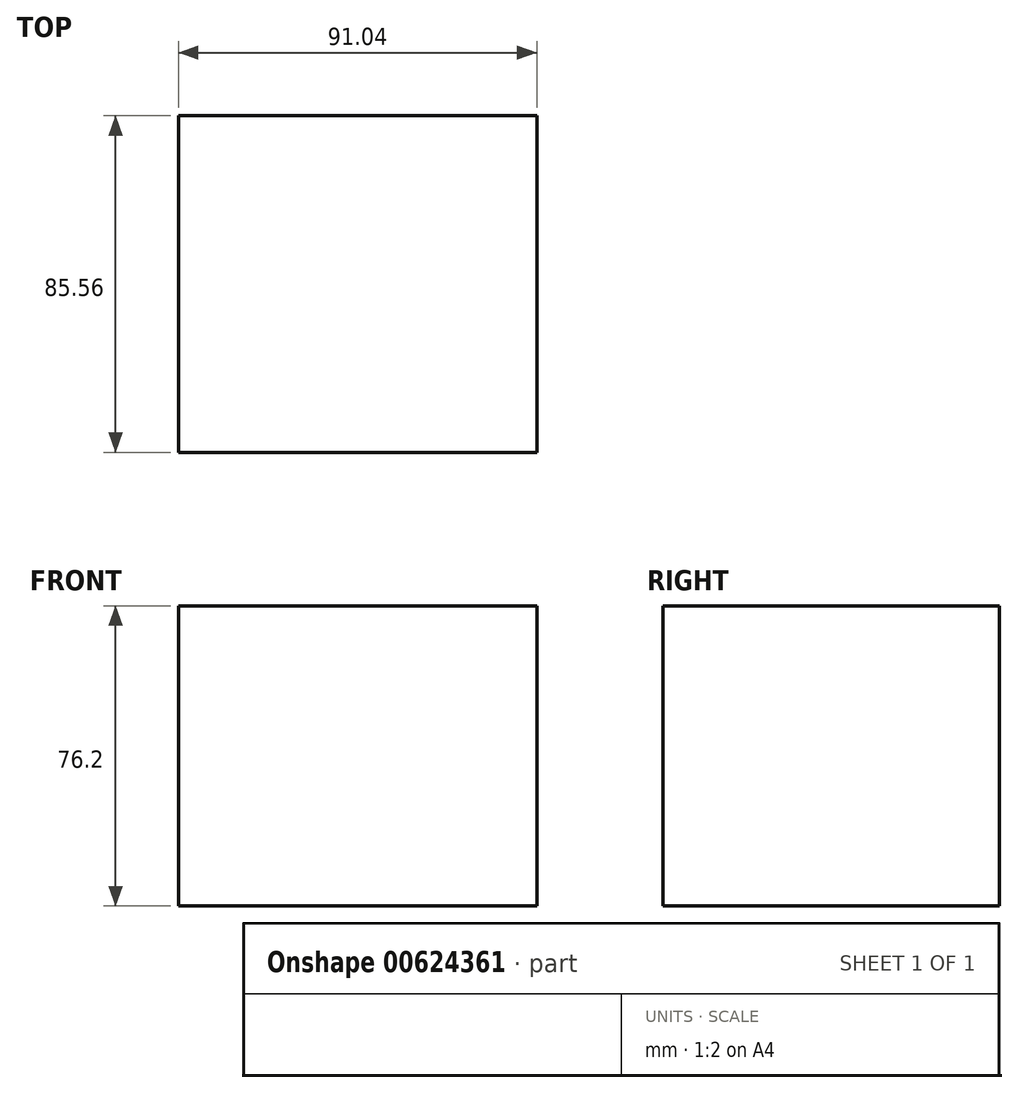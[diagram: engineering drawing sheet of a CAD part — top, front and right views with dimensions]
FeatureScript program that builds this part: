
annotation { "Feature Type Name" : "Feature", "Feature Type Description" : "" }
export const myFeature = defineFeature(function(context is Context, id is Id, definition is map)
    precondition{}
    {
        {
            var Q0;
            Q0=qCreatedBy(makeId("Top.planeOp"),FACE);
            var sketch = newSketch(context, id + "F0", { "sketchPlane" : qUnion([Q0])});
            skLineSegment(sketch, "E0.bottom", {"start": v(-45.52, -42.78) * mm, "end": v(45.52, -42.78) * mm});
            skLineSegment(sketch, "E0.top", {"start": v(-45.52, 42.78) * mm, "end": v(45.52, 42.78) * mm});
            skLineSegment(sketch, "E0.left", {"start": v(-45.52, -42.78) * mm, "end": v(-45.52, 42.78) * mm});
            skLineSegment(sketch, "E0.right", {"start": v(45.52, -42.78) * mm, "end": v(45.52, 42.78) * mm});
            skPoint(sketch, "E0.middle", {"position": v(0, 0) * mm});
            skSolve(sketch);
        }
        {
            var Q0;
            Q0 = qSketchRegion(id + "F0", true);
            extrude(context, id + "F1", {"entities" : qUnion([Q0]), "depth" : 76.2 * mm, "offsetDistance" : 25.4 * mm});
        }
    });
